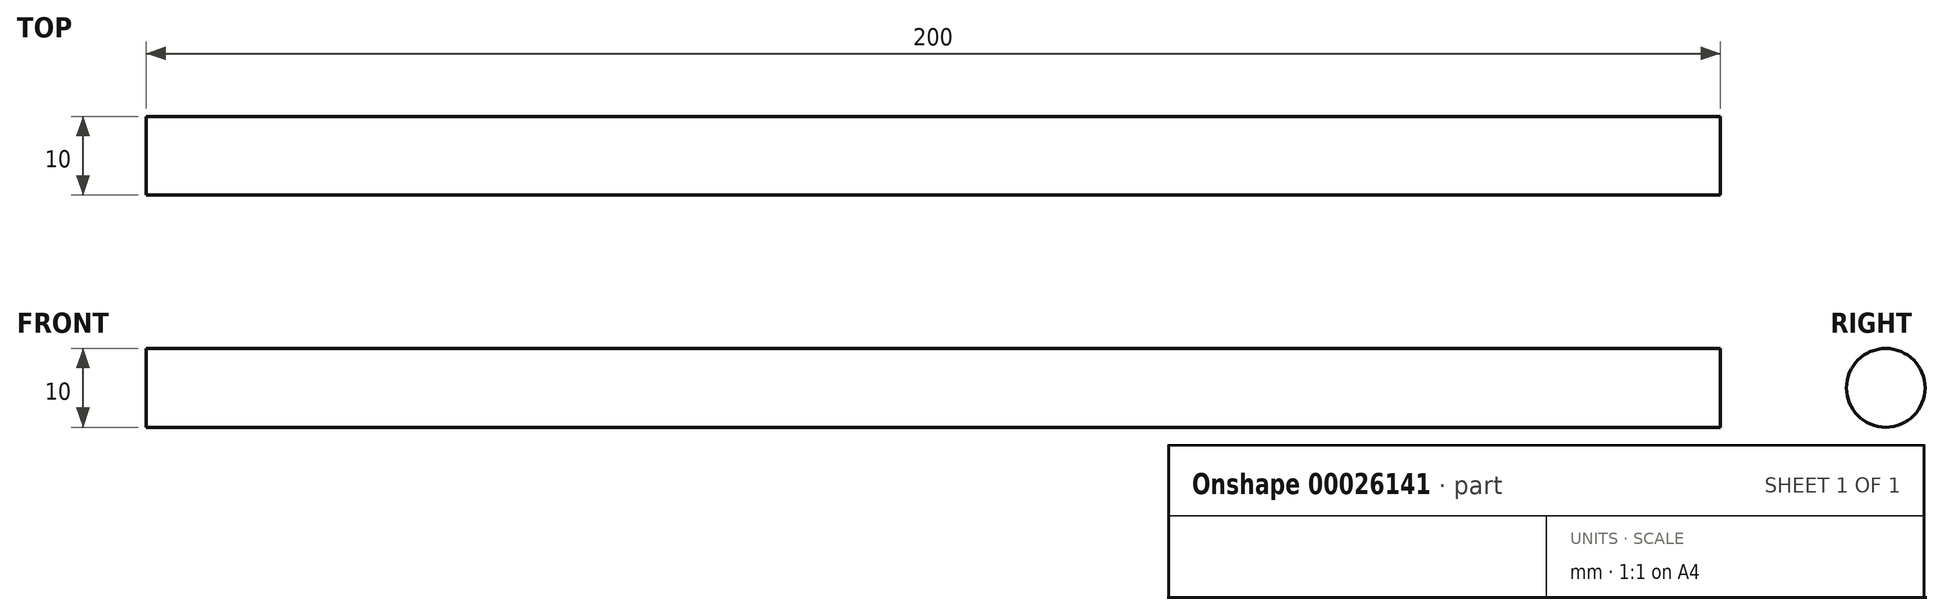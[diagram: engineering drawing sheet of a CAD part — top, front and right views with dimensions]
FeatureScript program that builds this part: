
annotation { "Feature Type Name" : "Feature", "Feature Type Description" : "" }
export const myFeature = defineFeature(function(context is Context, id is Id, definition is map)
    precondition{}
    {
        {
            var Q0;
            Q0=qCreatedBy(makeId("Right.planeOp"),FACE);
            var sketch = newSketch(context, id + "F0", { "sketchPlane" : qUnion([Q0])});
            skCircle(sketch, "E0", {"center": v(0, 0) * mm, "radius": 5 * mm});
            skSolve(sketch);
        }
        {
            var Q0;
            Q0=makeQuery(id+"F0.imprint","IMPRINT",FACE,{"disambiguationData":[TD([[makeQuery(id+"F0.imprint","IMPRINT",EDGE,{"derivedFrom":sQuery(id+"F0.wireOp",EDGE,"E0")}),1.0]])]});
            extrude(context, id + "F1", {"entities" : qUnion([Q0]), "depth" : 200 * mm});
        }
    });
